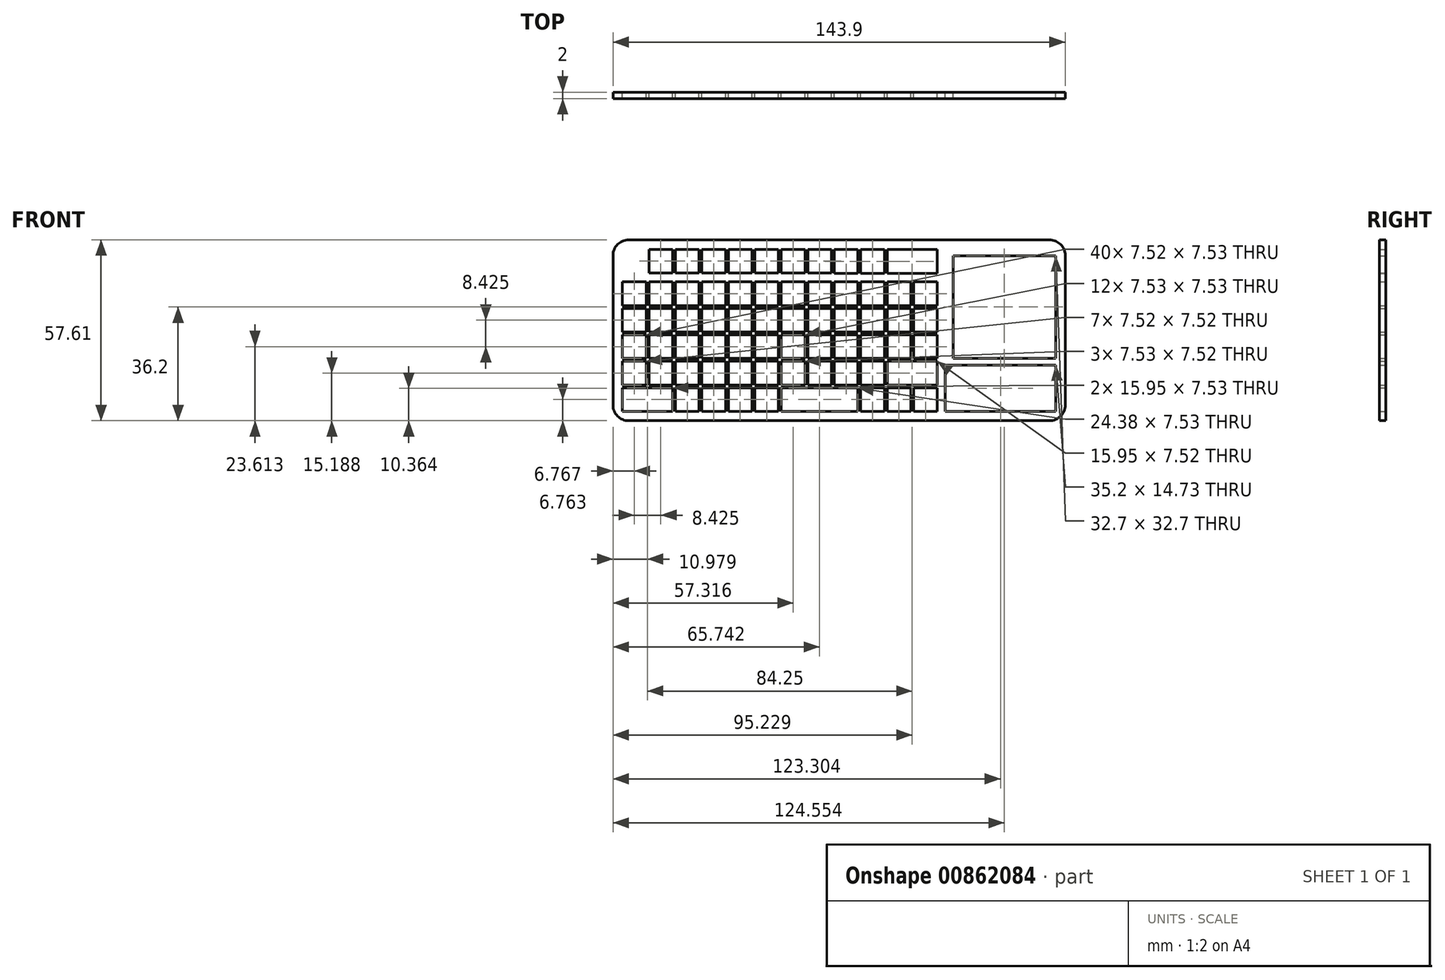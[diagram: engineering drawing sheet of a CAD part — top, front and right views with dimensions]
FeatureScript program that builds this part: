
annotation { "Feature Type Name" : "Feature", "Feature Type Description" : "" }
export const myFeature = defineFeature(function(context is Context, id is Id, definition is map)
    precondition{}
    {
        {
            var Q0;
            Q0=qCreatedBy(makeId("Front.planeOp"),FACE);
            var sketch = newSketch(context, id + "F0", { "sketchPlane" : qUnion([Q0])});
            skLineSegment(sketch, "E0.bottom", {"start": v(-54.97, 7.52) * mm, "end": v(-47.44, 7.52) * mm});
            skLineSegment(sketch, "E0.top", {"start": v(-54.97, 0) * mm, "end": v(-47.44, 0) * mm});
            skLineSegment(sketch, "E0.left", {"start": v(-54.97, 7.52) * mm, "end": v(-54.97, 0) * mm});
            skLineSegment(sketch, "E0.right", {"start": v(-47.44, 7.52) * mm, "end": v(-47.44, 0) * mm});
            skLineSegment(sketch, "E1.bottom", {"start": v(-46.54, 7.52) * mm, "end": v(-39.02, 7.52) * mm});
            skLineSegment(sketch, "E1.top", {"start": v(-46.54, 0) * mm, "end": v(-39.02, 0) * mm});
            skLineSegment(sketch, "E1.left", {"start": v(-46.54, 7.52) * mm, "end": v(-46.54, 0) * mm});
            skLineSegment(sketch, "E1.right", {"start": v(-39.02, 7.52) * mm, "end": v(-39.02, 0) * mm});
            skLineSegment(sketch, "E2.bottom", {"start": v(-29.7, 7.52) * mm, "end": v(-22.17, 7.52) * mm});
            skLineSegment(sketch, "E2.top", {"start": v(-29.7, 0) * mm, "end": v(-22.17, 0) * mm});
            skLineSegment(sketch, "E2.left", {"start": v(-29.7, 7.52) * mm, "end": v(-29.7, 0) * mm});
            skLineSegment(sketch, "E2.right", {"start": v(-22.17, 7.52) * mm, "end": v(-22.17, 0) * mm});
            skLineSegment(sketch, "E3.bottom", {"start": v(-38.12, 7.52) * mm, "end": v(-30.6, 7.52) * mm});
            skLineSegment(sketch, "E3.top", {"start": v(-38.12, 0) * mm, "end": v(-30.6, 0) * mm});
            skLineSegment(sketch, "E3.left", {"start": v(-38.12, 7.52) * mm, "end": v(-38.12, 0) * mm});
            skLineSegment(sketch, "E3.right", {"start": v(-30.6, 7.52) * mm, "end": v(-30.6, 0) * mm});
            skLineSegment(sketch, "E4.bottom", {"start": v(-21.27, 7.53) * mm, "end": v(-13.74, 7.53) * mm});
            skLineSegment(sketch, "E4.top", {"start": v(-21.27, 0) * mm, "end": v(-13.74, 0) * mm});
            skLineSegment(sketch, "E4.left", {"start": v(-21.27, 7.52) * mm, "end": v(-21.27, 0) * mm});
            skLineSegment(sketch, "E4.right", {"start": v(-13.74, 7.52) * mm, "end": v(-13.74, 0) * mm});
            skLineSegment(sketch, "E5.bottom", {"start": v(-12.84, 7.52) * mm, "end": v(-5.32, 7.52) * mm});
            skLineSegment(sketch, "E5.top", {"start": v(-12.84, 0) * mm, "end": v(-5.32, 0) * mm});
            skLineSegment(sketch, "E5.left", {"start": v(-12.84, 7.52) * mm, "end": v(-12.84, 0) * mm});
            skLineSegment(sketch, "E5.right", {"start": v(-5.32, 7.52) * mm, "end": v(-5.32, 0) * mm});
            skLineSegment(sketch, "E6.bottom", {"start": v(4, 7.52) * mm, "end": v(11.53, 7.52) * mm});
            skLineSegment(sketch, "E6.top", {"start": v(4, 0) * mm, "end": v(11.53, 0) * mm});
            skLineSegment(sketch, "E6.left", {"start": v(4, 7.52) * mm, "end": v(4, 0) * mm});
            skLineSegment(sketch, "E6.right", {"start": v(11.53, 7.53) * mm, "end": v(11.53, 0) * mm});
            skLineSegment(sketch, "E7.bottom", {"start": v(-4.42, 7.52) * mm, "end": v(3.1, 7.52) * mm});
            skLineSegment(sketch, "E7.top", {"start": v(-4.42, 0) * mm, "end": v(3.1, 0) * mm});
            skLineSegment(sketch, "E7.left", {"start": v(-4.42, 7.52) * mm, "end": v(-4.42, 0) * mm});
            skLineSegment(sketch, "E7.right", {"start": v(3.1, 7.53) * mm, "end": v(3.1, 0) * mm});
            skLineSegment(sketch, "E8.bottom", {"start": v(12.43, 7.52) * mm, "end": v(19.96, 7.52) * mm});
            skLineSegment(sketch, "E8.top", {"start": v(12.43, 0) * mm, "end": v(19.96, 0) * mm});
            skLineSegment(sketch, "E8.left", {"start": v(12.43, 7.52) * mm, "end": v(12.43, 0) * mm});
            skLineSegment(sketch, "E8.right", {"start": v(19.96, 7.52) * mm, "end": v(19.96, 0) * mm});
            skLineSegment(sketch, "E9.bottom", {"start": v(20.86, 7.52) * mm, "end": v(28.38, 7.52) * mm});
            skLineSegment(sketch, "E9.top", {"start": v(20.86, 0) * mm, "end": v(28.38, 0) * mm});
            skLineSegment(sketch, "E9.left", {"start": v(20.86, 7.52) * mm, "end": v(20.86, 0) * mm});
            skLineSegment(sketch, "E9.right", {"start": v(28.38, 7.52) * mm, "end": v(28.38, 0) * mm});
            skLineSegment(sketch, "E10.bottom", {"start": v(37.7, 7.52) * mm, "end": v(45.23, 7.52) * mm});
            skLineSegment(sketch, "E10.top", {"start": v(37.7, 0) * mm, "end": v(45.23, 0) * mm});
            skLineSegment(sketch, "E10.left", {"start": v(37.7, 7.52) * mm, "end": v(37.7, 0) * mm});
            skLineSegment(sketch, "E10.right", {"start": v(45.23, 7.52) * mm, "end": v(45.23, 0) * mm});
            skLineSegment(sketch, "E11.bottom", {"start": v(29.28, 7.53) * mm, "end": v(36.8, 7.53) * mm});
            skLineSegment(sketch, "E11.top", {"start": v(29.28, 0) * mm, "end": v(36.8, 0) * mm});
            skLineSegment(sketch, "E11.left", {"start": v(29.28, 7.53) * mm, "end": v(29.28, 0) * mm});
            skLineSegment(sketch, "E11.right", {"start": v(36.8, 7.52) * mm, "end": v(36.8, 0) * mm});
            skLineSegment(sketch, "E12.bottom", {"start": v(-54.97, -0.9) * mm, "end": v(-47.44, -0.9) * mm});
            skLineSegment(sketch, "E12.top", {"start": v(-54.97, -8.42) * mm, "end": v(-47.44, -8.42) * mm});
            skLineSegment(sketch, "E12.left", {"start": v(-54.97, -0.9) * mm, "end": v(-54.97, -8.43) * mm});
            skLineSegment(sketch, "E12.right", {"start": v(-47.44, -0.9) * mm, "end": v(-47.44, -8.42) * mm});
            skLineSegment(sketch, "E13.bottom", {"start": v(-46.54, -0.9) * mm, "end": v(-39.02, -0.9) * mm});
            skLineSegment(sketch, "E13.top", {"start": v(-46.54, -8.42) * mm, "end": v(-39.02, -8.42) * mm});
            skLineSegment(sketch, "E13.left", {"start": v(-46.54, -0.9) * mm, "end": v(-46.54, -8.42) * mm});
            skLineSegment(sketch, "E13.right", {"start": v(-39.02, -0.9) * mm, "end": v(-39.02, -8.42) * mm});
            skLineSegment(sketch, "E14.bottom", {"start": v(-29.7, -0.9) * mm, "end": v(-22.17, -0.9) * mm});
            skLineSegment(sketch, "E14.top", {"start": v(-29.7, -8.42) * mm, "end": v(-22.17, -8.42) * mm});
            skLineSegment(sketch, "E14.left", {"start": v(-29.7, -0.9) * mm, "end": v(-29.7, -8.42) * mm});
            skLineSegment(sketch, "E14.right", {"start": v(-22.17, -0.9) * mm, "end": v(-22.17, -8.42) * mm});
            skLineSegment(sketch, "E15.bottom", {"start": v(-38.12, -0.9) * mm, "end": v(-30.6, -0.9) * mm});
            skLineSegment(sketch, "E15.top", {"start": v(-38.12, -8.42) * mm, "end": v(-30.6, -8.42) * mm});
            skLineSegment(sketch, "E15.left", {"start": v(-38.12, -0.9) * mm, "end": v(-38.12, -8.42) * mm});
            skLineSegment(sketch, "E15.right", {"start": v(-30.6, -0.9) * mm, "end": v(-30.6, -8.42) * mm});
            skLineSegment(sketch, "E16.bottom", {"start": v(-21.27, -0.9) * mm, "end": v(-13.74, -0.9) * mm});
            skLineSegment(sketch, "E16.top", {"start": v(-21.27, -8.42) * mm, "end": v(-13.74, -8.42) * mm});
            skLineSegment(sketch, "E16.left", {"start": v(-21.27, -0.9) * mm, "end": v(-21.27, -8.42) * mm});
            skLineSegment(sketch, "E16.right", {"start": v(-13.74, -0.9) * mm, "end": v(-13.74, -8.42) * mm});
            skLineSegment(sketch, "E17.bottom", {"start": v(-12.84, -0.9) * mm, "end": v(-5.32, -0.9) * mm});
            skLineSegment(sketch, "E17.top", {"start": v(-12.84, -8.42) * mm, "end": v(-5.32, -8.42) * mm});
            skLineSegment(sketch, "E17.left", {"start": v(-12.84, -0.9) * mm, "end": v(-12.84, -8.42) * mm});
            skLineSegment(sketch, "E17.right", {"start": v(-5.32, -0.9) * mm, "end": v(-5.32, -8.42) * mm});
            skLineSegment(sketch, "E18.bottom", {"start": v(4, -0.9) * mm, "end": v(11.53, -0.9) * mm});
            skLineSegment(sketch, "E18.top", {"start": v(4, -8.42) * mm, "end": v(11.53, -8.42) * mm});
            skLineSegment(sketch, "E18.left", {"start": v(4, -0.9) * mm, "end": v(4, -8.42) * mm});
            skLineSegment(sketch, "E18.right", {"start": v(11.53, -0.9) * mm, "end": v(11.53, -8.42) * mm});
            skLineSegment(sketch, "E19.bottom", {"start": v(-4.42, -0.9) * mm, "end": v(3.1, -0.9) * mm});
            skLineSegment(sketch, "E19.top", {"start": v(-4.42, -8.42) * mm, "end": v(3.1, -8.42) * mm});
            skLineSegment(sketch, "E19.left", {"start": v(-4.42, -0.9) * mm, "end": v(-4.42, -8.42) * mm});
            skLineSegment(sketch, "E19.right", {"start": v(3.1, -0.9) * mm, "end": v(3.1, -8.42) * mm});
            skLineSegment(sketch, "E20.bottom", {"start": v(12.43, -0.9) * mm, "end": v(19.96, -0.9) * mm});
            skLineSegment(sketch, "E20.top", {"start": v(12.43, -8.42) * mm, "end": v(19.96, -8.42) * mm});
            skLineSegment(sketch, "E20.left", {"start": v(12.43, -0.9) * mm, "end": v(12.43, -8.42) * mm});
            skLineSegment(sketch, "E20.right", {"start": v(19.96, -0.9) * mm, "end": v(19.96, -8.42) * mm});
            skLineSegment(sketch, "E21.bottom", {"start": v(20.86, -0.9) * mm, "end": v(28.38, -0.9) * mm});
            skLineSegment(sketch, "E21.top", {"start": v(20.86, -8.42) * mm, "end": v(28.38, -8.42) * mm});
            skLineSegment(sketch, "E21.left", {"start": v(20.86, -0.9) * mm, "end": v(20.86, -8.42) * mm});
            skLineSegment(sketch, "E21.right", {"start": v(28.38, -0.9) * mm, "end": v(28.38, -8.42) * mm});
            skLineSegment(sketch, "E22.bottom", {"start": v(37.7, -0.9) * mm, "end": v(45.23, -0.9) * mm});
            skLineSegment(sketch, "E22.top", {"start": v(37.7, -8.42) * mm, "end": v(45.23, -8.42) * mm});
            skLineSegment(sketch, "E22.left", {"start": v(37.7, -0.9) * mm, "end": v(37.7, -8.42) * mm});
            skLineSegment(sketch, "E22.right", {"start": v(45.23, -0.9) * mm, "end": v(45.23, -8.42) * mm});
            skLineSegment(sketch, "E23.bottom", {"start": v(29.28, -0.9) * mm, "end": v(36.8, -0.9) * mm});
            skLineSegment(sketch, "E23.top", {"start": v(29.28, -8.42) * mm, "end": v(36.8, -8.42) * mm});
            skLineSegment(sketch, "E23.left", {"start": v(29.28, -0.9) * mm, "end": v(29.28, -8.42) * mm});
            skLineSegment(sketch, "E23.right", {"start": v(36.8, -0.9) * mm, "end": v(36.8, -8.42) * mm});
            skLineSegment(sketch, "E24", {"start": v(-54.97, -8.42) * mm, "end": v(45.23, -8.42) * mm});
            skLineSegment(sketch, "E25.bottom", {"start": v(-54.97, -9.32) * mm, "end": v(-47.44, -9.32) * mm});
            skLineSegment(sketch, "E25.top", {"start": v(-54.97, -16.85) * mm, "end": v(-47.44, -16.85) * mm});
            skLineSegment(sketch, "E25.left", {"start": v(-54.97, -9.32) * mm, "end": v(-54.97, -16.85) * mm});
            skLineSegment(sketch, "E25.right", {"start": v(-47.44, -9.32) * mm, "end": v(-47.44, -16.85) * mm});
            skLineSegment(sketch, "E26.bottom", {"start": v(-46.54, -9.32) * mm, "end": v(-39.02, -9.32) * mm});
            skLineSegment(sketch, "E26.top", {"start": v(-46.54, -16.85) * mm, "end": v(-39.02, -16.85) * mm});
            skLineSegment(sketch, "E26.left", {"start": v(-46.54, -9.32) * mm, "end": v(-46.54, -16.85) * mm});
            skLineSegment(sketch, "E26.right", {"start": v(-39.02, -9.32) * mm, "end": v(-39.02, -16.85) * mm});
            skLineSegment(sketch, "E27.bottom", {"start": v(-29.7, -9.32) * mm, "end": v(-22.17, -9.32) * mm});
            skLineSegment(sketch, "E27.top", {"start": v(-29.7, -16.85) * mm, "end": v(-22.17, -16.85) * mm});
            skLineSegment(sketch, "E27.left", {"start": v(-29.7, -9.32) * mm, "end": v(-29.7, -16.85) * mm});
            skLineSegment(sketch, "E27.right", {"start": v(-22.17, -9.32) * mm, "end": v(-22.17, -16.85) * mm});
            skLineSegment(sketch, "E28.bottom", {"start": v(-38.12, -9.32) * mm, "end": v(-30.6, -9.32) * mm});
            skLineSegment(sketch, "E28.top", {"start": v(-38.12, -16.85) * mm, "end": v(-30.6, -16.85) * mm});
            skLineSegment(sketch, "E28.left", {"start": v(-38.12, -9.32) * mm, "end": v(-38.12, -16.85) * mm});
            skLineSegment(sketch, "E28.right", {"start": v(-30.6, -9.32) * mm, "end": v(-30.6, -16.85) * mm});
            skLineSegment(sketch, "E29.bottom", {"start": v(-21.27, -9.32) * mm, "end": v(-13.74, -9.32) * mm});
            skLineSegment(sketch, "E29.top", {"start": v(-21.27, -16.85) * mm, "end": v(-13.74, -16.85) * mm});
            skLineSegment(sketch, "E29.left", {"start": v(-21.27, -9.32) * mm, "end": v(-21.27, -16.85) * mm});
            skLineSegment(sketch, "E29.right", {"start": v(-13.74, -9.32) * mm, "end": v(-13.74, -16.85) * mm});
            skLineSegment(sketch, "E30.bottom", {"start": v(-12.84, -9.32) * mm, "end": v(-5.32, -9.32) * mm});
            skLineSegment(sketch, "E30.top", {"start": v(-12.84, -16.85) * mm, "end": v(-5.32, -16.85) * mm});
            skLineSegment(sketch, "E30.left", {"start": v(-12.84, -9.32) * mm, "end": v(-12.84, -16.85) * mm});
            skLineSegment(sketch, "E30.right", {"start": v(-5.32, -9.32) * mm, "end": v(-5.32, -16.85) * mm});
            skLineSegment(sketch, "E31.bottom", {"start": v(4, -9.32) * mm, "end": v(11.53, -9.32) * mm});
            skLineSegment(sketch, "E31.top", {"start": v(4, -16.85) * mm, "end": v(11.53, -16.85) * mm});
            skLineSegment(sketch, "E31.left", {"start": v(4, -9.32) * mm, "end": v(4, -16.85) * mm});
            skLineSegment(sketch, "E31.right", {"start": v(11.53, -9.32) * mm, "end": v(11.53, -16.85) * mm});
            skLineSegment(sketch, "E32.bottom", {"start": v(-4.42, -9.32) * mm, "end": v(3.1, -9.32) * mm});
            skLineSegment(sketch, "E32.top", {"start": v(-4.42, -16.85) * mm, "end": v(3.1, -16.85) * mm});
            skLineSegment(sketch, "E32.left", {"start": v(-4.42, -9.32) * mm, "end": v(-4.42, -16.85) * mm});
            skLineSegment(sketch, "E32.right", {"start": v(3.1, -9.32) * mm, "end": v(3.1, -16.85) * mm});
            skLineSegment(sketch, "E33.bottom", {"start": v(12.43, -9.32) * mm, "end": v(19.96, -9.32) * mm});
            skLineSegment(sketch, "E33.top", {"start": v(12.43, -16.85) * mm, "end": v(19.96, -16.85) * mm});
            skLineSegment(sketch, "E33.left", {"start": v(12.43, -9.32) * mm, "end": v(12.43, -16.85) * mm});
            skLineSegment(sketch, "E33.right", {"start": v(19.96, -9.32) * mm, "end": v(19.96, -16.85) * mm});
            skLineSegment(sketch, "E34.bottom", {"start": v(20.86, -9.32) * mm, "end": v(28.38, -9.32) * mm});
            skLineSegment(sketch, "E34.top", {"start": v(20.86, -16.85) * mm, "end": v(28.38, -16.85) * mm});
            skLineSegment(sketch, "E34.left", {"start": v(20.86, -9.32) * mm, "end": v(20.86, -16.85) * mm});
            skLineSegment(sketch, "E34.right", {"start": v(28.38, -9.32) * mm, "end": v(28.38, -16.85) * mm});
            skLineSegment(sketch, "E35.bottom", {"start": v(37.7, -9.32) * mm, "end": v(45.23, -9.32) * mm});
            skLineSegment(sketch, "E35.top", {"start": v(37.7, -16.85) * mm, "end": v(45.23, -16.85) * mm});
            skLineSegment(sketch, "E35.left", {"start": v(37.7, -9.32) * mm, "end": v(37.7, -16.85) * mm});
            skLineSegment(sketch, "E35.right", {"start": v(45.23, -9.32) * mm, "end": v(45.23, -16.85) * mm});
            skLineSegment(sketch, "E36.bottom", {"start": v(29.28, -9.32) * mm, "end": v(36.8, -9.32) * mm});
            skLineSegment(sketch, "E36.top", {"start": v(29.28, -16.85) * mm, "end": v(36.8, -16.85) * mm});
            skLineSegment(sketch, "E36.left", {"start": v(29.28, -9.32) * mm, "end": v(29.28, -16.85) * mm});
            skLineSegment(sketch, "E36.right", {"start": v(36.8, -9.32) * mm, "end": v(36.8, -16.85) * mm});
            skLineSegment(sketch, "E37", {"start": v(-54.97, -16.85) * mm, "end": v(45.23, -16.85) * mm});
            skLineSegment(sketch, "E38.bottom", {"start": v(-54.97, -17.75) * mm, "end": v(-47.44, -17.75) * mm});
            skLineSegment(sketch, "E38.top", {"start": v(-54.97, -25.27) * mm, "end": v(-47.44, -25.27) * mm});
            skLineSegment(sketch, "E38.left", {"start": v(-54.97, -17.75) * mm, "end": v(-54.97, -25.27) * mm});
            skLineSegment(sketch, "E38.right", {"start": v(-47.44, -17.75) * mm, "end": v(-47.44, -25.27) * mm});
            skLineSegment(sketch, "E39.bottom", {"start": v(-46.54, -17.75) * mm, "end": v(-39.02, -17.75) * mm});
            skLineSegment(sketch, "E39.top", {"start": v(-46.54, -25.27) * mm, "end": v(-39.02, -25.27) * mm});
            skLineSegment(sketch, "E39.left", {"start": v(-46.54, -17.75) * mm, "end": v(-46.54, -25.28) * mm});
            skLineSegment(sketch, "E39.right", {"start": v(-39.02, -17.75) * mm, "end": v(-39.02, -25.28) * mm});
            skLineSegment(sketch, "E40.bottom", {"start": v(-29.7, -17.75) * mm, "end": v(-22.17, -17.75) * mm});
            skLineSegment(sketch, "E40.top", {"start": v(-29.7, -25.27) * mm, "end": v(-22.17, -25.27) * mm});
            skLineSegment(sketch, "E40.left", {"start": v(-29.7, -17.75) * mm, "end": v(-29.7, -25.27) * mm});
            skLineSegment(sketch, "E40.right", {"start": v(-22.17, -17.75) * mm, "end": v(-22.17, -25.27) * mm});
            skLineSegment(sketch, "E41.bottom", {"start": v(-38.12, -17.75) * mm, "end": v(-30.6, -17.75) * mm});
            skLineSegment(sketch, "E41.top", {"start": v(-38.12, -25.27) * mm, "end": v(-30.6, -25.27) * mm});
            skLineSegment(sketch, "E41.left", {"start": v(-38.12, -17.75) * mm, "end": v(-38.12, -25.27) * mm});
            skLineSegment(sketch, "E41.right", {"start": v(-30.6, -17.75) * mm, "end": v(-30.6, -25.27) * mm});
            skLineSegment(sketch, "E42.bottom", {"start": v(-21.27, -17.75) * mm, "end": v(-13.74, -17.75) * mm});
            skLineSegment(sketch, "E42.top", {"start": v(-21.27, -25.27) * mm, "end": v(-13.74, -25.27) * mm});
            skLineSegment(sketch, "E42.left", {"start": v(-21.27, -17.75) * mm, "end": v(-21.27, -25.27) * mm});
            skLineSegment(sketch, "E42.right", {"start": v(-13.74, -17.75) * mm, "end": v(-13.74, -25.27) * mm});
            skLineSegment(sketch, "E43.bottom", {"start": v(-12.84, -17.75) * mm, "end": v(-5.32, -17.75) * mm});
            skLineSegment(sketch, "E43.top", {"start": v(-12.84, -25.27) * mm, "end": v(-5.32, -25.27) * mm});
            skLineSegment(sketch, "E43.left", {"start": v(-12.84, -17.75) * mm, "end": v(-12.84, -25.27) * mm});
            skLineSegment(sketch, "E43.right", {"start": v(-5.32, -17.75) * mm, "end": v(-5.32, -25.27) * mm});
            skLineSegment(sketch, "E44.bottom", {"start": v(4, -17.75) * mm, "end": v(11.53, -17.75) * mm});
            skLineSegment(sketch, "E44.top", {"start": v(4, -25.27) * mm, "end": v(11.53, -25.27) * mm});
            skLineSegment(sketch, "E44.left", {"start": v(4, -17.75) * mm, "end": v(4, -25.27) * mm});
            skLineSegment(sketch, "E44.right", {"start": v(11.53, -17.75) * mm, "end": v(11.53, -25.27) * mm});
            skLineSegment(sketch, "E45.bottom", {"start": v(-4.42, -17.75) * mm, "end": v(3.1, -17.75) * mm});
            skLineSegment(sketch, "E45.top", {"start": v(-4.42, -25.27) * mm, "end": v(3.1, -25.27) * mm});
            skLineSegment(sketch, "E45.left", {"start": v(-4.42, -17.75) * mm, "end": v(-4.42, -25.27) * mm});
            skLineSegment(sketch, "E45.right", {"start": v(3.1, -17.75) * mm, "end": v(3.1, -25.27) * mm});
            skLineSegment(sketch, "E46.bottom", {"start": v(12.43, -17.75) * mm, "end": v(19.96, -17.75) * mm});
            skLineSegment(sketch, "E46.top", {"start": v(12.43, -25.27) * mm, "end": v(19.96, -25.27) * mm});
            skLineSegment(sketch, "E46.left", {"start": v(12.43, -17.75) * mm, "end": v(12.43, -25.27) * mm});
            skLineSegment(sketch, "E46.right", {"start": v(19.96, -17.75) * mm, "end": v(19.96, -25.27) * mm});
            skLineSegment(sketch, "E47.bottom", {"start": v(20.86, -17.75) * mm, "end": v(28.38, -17.75) * mm});
            skLineSegment(sketch, "E47.top", {"start": v(20.86, -25.27) * mm, "end": v(28.38, -25.27) * mm});
            skLineSegment(sketch, "E47.left", {"start": v(20.86, -17.75) * mm, "end": v(20.86, -25.27) * mm});
            skLineSegment(sketch, "E47.right", {"start": v(28.38, -17.75) * mm, "end": v(28.38, -25.27) * mm});
            skLineSegment(sketch, "E48.top", {"start": v(37.7, -25.27) * mm, "end": v(45.23, -25.27) * mm});
            skLineSegment(sketch, "E48.right", {"start": v(45.23, -17.75) * mm, "end": v(45.23, -25.28) * mm});
            skLineSegment(sketch, "E49.top", {"start": v(29.28, -25.27) * mm, "end": v(36.8, -25.27) * mm});
            skLineSegment(sketch, "E49.left", {"start": v(29.28, -17.75) * mm, "end": v(29.28, -25.27) * mm});
            skLineSegment(sketch, "E50", {"start": v(-54.97, -25.27) * mm, "end": v(45.23, -25.27) * mm});
            skLineSegment(sketch, "E51.top", {"start": v(-54.97, -33.7) * mm, "end": v(-47.44, -33.7) * mm});
            skLineSegment(sketch, "E51.left", {"start": v(-54.97, -26.17) * mm, "end": v(-54.97, -33.7) * mm});
            skLineSegment(sketch, "E52.top", {"start": v(-46.54, -33.7) * mm, "end": v(-39.02, -33.7) * mm});
            skLineSegment(sketch, "E52.right", {"start": v(-39.02, -26.17) * mm, "end": v(-39.02, -33.7) * mm});
            skLineSegment(sketch, "E53.bottom", {"start": v(-29.7, -26.17) * mm, "end": v(-22.17, -26.17) * mm});
            skLineSegment(sketch, "E53.top", {"start": v(-29.7, -33.7) * mm, "end": v(-22.17, -33.7) * mm});
            skLineSegment(sketch, "E53.left", {"start": v(-29.7, -26.17) * mm, "end": v(-29.7, -33.7) * mm});
            skLineSegment(sketch, "E53.right", {"start": v(-22.17, -26.17) * mm, "end": v(-22.17, -33.7) * mm});
            skLineSegment(sketch, "E54.bottom", {"start": v(-38.12, -26.17) * mm, "end": v(-30.6, -26.17) * mm});
            skLineSegment(sketch, "E54.top", {"start": v(-38.12, -33.7) * mm, "end": v(-30.6, -33.7) * mm});
            skLineSegment(sketch, "E54.left", {"start": v(-38.12, -26.17) * mm, "end": v(-38.12, -33.7) * mm});
            skLineSegment(sketch, "E54.right", {"start": v(-30.6, -26.17) * mm, "end": v(-30.6, -33.7) * mm});
            skLineSegment(sketch, "E55.bottom", {"start": v(-21.27, -26.17) * mm, "end": v(-13.74, -26.17) * mm});
            skLineSegment(sketch, "E55.top", {"start": v(-21.27, -33.7) * mm, "end": v(-13.74, -33.7) * mm});
            skLineSegment(sketch, "E55.left", {"start": v(-21.27, -26.17) * mm, "end": v(-21.27, -33.7) * mm});
            skLineSegment(sketch, "E55.right", {"start": v(-13.74, -26.17) * mm, "end": v(-13.74, -33.7) * mm});
            skLineSegment(sketch, "E56.bottom", {"start": v(-12.84, -26.17) * mm, "end": v(-5.32, -26.17) * mm});
            skLineSegment(sketch, "E56.top", {"start": v(-12.84, -33.7) * mm, "end": v(-5.32, -33.7) * mm});
            skLineSegment(sketch, "E56.left", {"start": v(-12.84, -26.17) * mm, "end": v(-12.84, -33.7) * mm});
            skLineSegment(sketch, "E56.right", {"start": v(-5.32, -26.17) * mm, "end": v(-5.32, -33.7) * mm});
            skLineSegment(sketch, "E57.top", {"start": v(4, -33.7) * mm, "end": v(11.53, -33.7) * mm});
            skLineSegment(sketch, "E58.top", {"start": v(-4.42, -33.7) * mm, "end": v(3.1, -33.7) * mm});
            skLineSegment(sketch, "E58.left", {"start": v(-4.42, -26.17) * mm, "end": v(-4.42, -33.7) * mm});
            skLineSegment(sketch, "E59.top", {"start": v(12.43, -33.7) * mm, "end": v(19.96, -33.7) * mm});
            skLineSegment(sketch, "E59.right", {"start": v(19.96, -26.17) * mm, "end": v(19.96, -33.7) * mm});
            skLineSegment(sketch, "E60.bottom", {"start": v(20.86, -26.17) * mm, "end": v(28.38, -26.17) * mm});
            skLineSegment(sketch, "E60.top", {"start": v(20.86, -33.7) * mm, "end": v(28.38, -33.7) * mm});
            skLineSegment(sketch, "E60.left", {"start": v(20.86, -26.17) * mm, "end": v(20.86, -33.7) * mm});
            skLineSegment(sketch, "E60.right", {"start": v(28.38, -26.17) * mm, "end": v(28.38, -33.7) * mm});
            skLineSegment(sketch, "E61.bottom", {"start": v(37.7, -26.17) * mm, "end": v(45.23, -26.17) * mm});
            skLineSegment(sketch, "E61.top", {"start": v(37.7, -33.7) * mm, "end": v(45.23, -33.7) * mm});
            skLineSegment(sketch, "E61.left", {"start": v(37.7, -26.17) * mm, "end": v(37.7, -33.7) * mm});
            skLineSegment(sketch, "E61.right", {"start": v(45.23, -26.17) * mm, "end": v(45.23, -33.7) * mm});
            skLineSegment(sketch, "E62.bottom", {"start": v(29.28, -26.17) * mm, "end": v(36.8, -26.18) * mm});
            skLineSegment(sketch, "E62.top", {"start": v(29.28, -33.7) * mm, "end": v(36.8, -33.7) * mm});
            skLineSegment(sketch, "E62.left", {"start": v(29.28, -26.17) * mm, "end": v(29.28, -33.7) * mm});
            skLineSegment(sketch, "E62.right", {"start": v(36.8, -26.17) * mm, "end": v(36.8, -33.7) * mm});
            skLineSegment(sketch, "E63", {"start": v(-54.97, -33.7) * mm, "end": v(45.23, -33.7) * mm});
            skLineSegment(sketch, "E64", {"start": v(45.23, 7.53) * mm, "end": v(45.23, -33.7) * mm});
            skLineSegment(sketch, "E65.bottom", {"start": v(-46.54, 17.9) * mm, "end": v(-39.02, 17.9) * mm});
            skLineSegment(sketch, "E65.top", {"start": v(-46.54, 10.38) * mm, "end": v(-39.02, 10.38) * mm});
            skLineSegment(sketch, "E65.left", {"start": v(-46.54, 17.9) * mm, "end": v(-46.54, 10.38) * mm});
            skLineSegment(sketch, "E65.right", {"start": v(-39.02, 17.9) * mm, "end": v(-39.02, 10.38) * mm});
            skLineSegment(sketch, "E66.bottom", {"start": v(-29.7, 17.9) * mm, "end": v(-22.17, 17.9) * mm});
            skLineSegment(sketch, "E66.top", {"start": v(-29.7, 10.38) * mm, "end": v(-22.17, 10.38) * mm});
            skLineSegment(sketch, "E66.left", {"start": v(-29.7, 17.9) * mm, "end": v(-29.7, 10.38) * mm});
            skLineSegment(sketch, "E66.right", {"start": v(-22.17, 17.9) * mm, "end": v(-22.17, 10.38) * mm});
            skLineSegment(sketch, "E67.bottom", {"start": v(-38.12, 17.9) * mm, "end": v(-30.6, 17.9) * mm});
            skLineSegment(sketch, "E67.top", {"start": v(-38.12, 10.38) * mm, "end": v(-30.6, 10.38) * mm});
            skLineSegment(sketch, "E67.left", {"start": v(-38.12, 17.9) * mm, "end": v(-38.12, 10.38) * mm});
            skLineSegment(sketch, "E67.right", {"start": v(-30.6, 17.9) * mm, "end": v(-30.6, 10.38) * mm});
            skLineSegment(sketch, "E68.bottom", {"start": v(-21.27, 17.9) * mm, "end": v(-13.74, 17.9) * mm});
            skLineSegment(sketch, "E68.top", {"start": v(-21.27, 10.38) * mm, "end": v(-13.74, 10.38) * mm});
            skLineSegment(sketch, "E68.left", {"start": v(-21.27, 17.9) * mm, "end": v(-21.27, 10.38) * mm});
            skLineSegment(sketch, "E68.right", {"start": v(-13.74, 17.9) * mm, "end": v(-13.74, 10.38) * mm});
            skLineSegment(sketch, "E69.bottom", {"start": v(-12.84, 17.9) * mm, "end": v(-5.32, 17.9) * mm});
            skLineSegment(sketch, "E69.top", {"start": v(-12.84, 10.38) * mm, "end": v(-5.32, 10.38) * mm});
            skLineSegment(sketch, "E69.left", {"start": v(-12.84, 17.9) * mm, "end": v(-12.84, 10.38) * mm});
            skLineSegment(sketch, "E69.right", {"start": v(-5.32, 17.9) * mm, "end": v(-5.32, 10.38) * mm});
            skLineSegment(sketch, "E70.bottom", {"start": v(4, 17.9) * mm, "end": v(11.53, 17.9) * mm});
            skLineSegment(sketch, "E70.top", {"start": v(4, 10.38) * mm, "end": v(11.53, 10.38) * mm});
            skLineSegment(sketch, "E70.left", {"start": v(4, 17.9) * mm, "end": v(4, 10.38) * mm});
            skLineSegment(sketch, "E70.right", {"start": v(11.53, 17.9) * mm, "end": v(11.53, 10.38) * mm});
            skLineSegment(sketch, "E71.bottom", {"start": v(-4.42, 17.9) * mm, "end": v(3.1, 17.9) * mm});
            skLineSegment(sketch, "E71.top", {"start": v(-4.42, 10.38) * mm, "end": v(3.1, 10.38) * mm});
            skLineSegment(sketch, "E71.left", {"start": v(-4.42, 17.9) * mm, "end": v(-4.42, 10.38) * mm});
            skLineSegment(sketch, "E71.right", {"start": v(3.1, 17.9) * mm, "end": v(3.1, 10.38) * mm});
            skLineSegment(sketch, "E72.bottom", {"start": v(12.43, 17.8) * mm, "end": v(19.96, 17.8) * mm});
            skLineSegment(sketch, "E72.top", {"start": v(12.43, 10.27) * mm, "end": v(19.96, 10.27) * mm});
            skLineSegment(sketch, "E72.left", {"start": v(12.43, 17.8) * mm, "end": v(12.43, 10.27) * mm});
            skLineSegment(sketch, "E72.right", {"start": v(19.96, 17.8) * mm, "end": v(19.96, 10.27) * mm});
            skLineSegment(sketch, "E73.bottom", {"start": v(20.86, 17.8) * mm, "end": v(28.38, 17.8) * mm});
            skLineSegment(sketch, "E73.top", {"start": v(20.86, 10.27) * mm, "end": v(28.38, 10.27) * mm});
            skLineSegment(sketch, "E73.left", {"start": v(20.86, 17.8) * mm, "end": v(20.86, 10.27) * mm});
            skLineSegment(sketch, "E73.right", {"start": v(28.38, 17.8) * mm, "end": v(28.38, 10.27) * mm});
            skLineSegment(sketch, "E74.bottom", {"start": v(37.7, 17.8) * mm, "end": v(45.23, 17.8) * mm});
            skLineSegment(sketch, "E74.top", {"start": v(37.7, 10.27) * mm, "end": v(45.23, 10.27) * mm});
            skLineSegment(sketch, "E74.right", {"start": v(45.23, 17.8) * mm, "end": v(45.23, 10.27) * mm});
            skLineSegment(sketch, "E75.bottom", {"start": v(29.28, 17.8) * mm, "end": v(36.8, 17.8) * mm});
            skLineSegment(sketch, "E75.top", {"start": v(29.28, 10.27) * mm, "end": v(36.8, 10.27) * mm});
            skLineSegment(sketch, "E75.left", {"start": v(29.28, 17.8) * mm, "end": v(29.28, 10.27) * mm});
            skLineSegment(sketch, "E76", {"start": v(-46.54, 10.38) * mm, "end": v(45.23, 10.27) * mm});
            skLineSegment(sketch, "E77", {"start": v(36.8, 17.8) * mm, "end": v(37.7, 17.8) * mm});
            skLineSegment(sketch, "E78", {"start": v(36.8, 10.27) * mm, "end": v(37.7, 10.27) * mm});
            skLineSegment(sketch, "E79", {"start": v(29.28, -17.75) * mm, "end": v(45.23, -17.75) * mm});
            skLineSegment(sketch, "E80", {"start": v(-54.97, -26.17) * mm, "end": v(-39.02, -26.17) * mm});
            skLineSegment(sketch, "E81", {"start": v(-4.42, -26.17) * mm, "end": v(19.96, -26.17) * mm});
            skLineSegment(sketch, "E82.bottom", {"start": v(50.23, 15.85) * mm, "end": v(82.93, 15.85) * mm});
            skLineSegment(sketch, "E82.top", {"start": v(50.23, -16.85) * mm, "end": v(82.93, -16.85) * mm});
            skLineSegment(sketch, "E82.left", {"start": v(50.23, 15.85) * mm, "end": v(50.23, -16.85) * mm});
            skLineSegment(sketch, "E82.right", {"start": v(82.93, 15.85) * mm, "end": v(82.93, -16.85) * mm});
            skLineSegment(sketch, "E83", {"start": v(50.23, -16.85) * mm, "end": v(45.23, -16.85) * mm});
            skLineSegment(sketch, "E84.bottom", {"start": v(-57.97, 20.9) * mm, "end": v(85.93, 20.9) * mm});
            skLineSegment(sketch, "E84.top", {"start": v(-57.97, -36.7) * mm, "end": v(85.93, -36.7) * mm});
            skLineSegment(sketch, "E84.left", {"start": v(-57.97, 20.9) * mm, "end": v(-57.97, -36.7) * mm});
            skLineSegment(sketch, "E84.right", {"start": v(85.93, 20.9) * mm, "end": v(85.93, -36.7) * mm});
            skLineSegment(sketch, "E85.bottom", {"start": v(47.73, -16.85) * mm, "end": v(82.93, -16.85) * mm});
            skLineSegment(sketch, "E86.bottom", {"start": v(47.73, -18.97) * mm, "end": v(82.93, -18.97) * mm});
            skLineSegment(sketch, "E86.top", {"start": v(47.73, -33.7) * mm, "end": v(82.93, -33.7) * mm});
            skLineSegment(sketch, "E86.left", {"start": v(47.73, -18.97) * mm, "end": v(47.73, -33.7) * mm});
            skLineSegment(sketch, "E86.right", {"start": v(82.93, -18.97) * mm, "end": v(82.93, -33.7) * mm});
            skLineSegment(sketch, "E87", {"start": v(47.73, -16.85) * mm, "end": v(47.73, -18.97) * mm});
            skSolve(sketch);
        }
        {
            var Q0;
            Q0 = qSketchRegion(id + "F0", true);
            extrude(context, id + "F1", {"entities" : qUnion([Q0]), "depth" : 2 * mm, "offsetDistance" : 25 * mm});
        }
        {
            var Q0;
            Q0=makeQuery(id+"F1.opExtrude","SWEPT_EDGE",EDGE,{"disambiguationData":[OSD([sQuery(id+"F0.wireOp",EDGE,"E84.bottom"),sQuery(id+"F0.wireOp",EDGE,"E84.left")])]});
            var Q1;
            Q1=makeQuery(id+"F1.opExtrude","SWEPT_EDGE",EDGE,{"disambiguationData":[OSD([sQuery(id+"F0.wireOp",EDGE,"E84.bottom"),sQuery(id+"F0.wireOp",EDGE,"E84.right")])]});
            var Q2;
            Q2=makeQuery(id+"F1.opExtrude","SWEPT_EDGE",EDGE,{"disambiguationData":[OSD([sQuery(id+"F0.wireOp",EDGE,"E84.top"),sQuery(id+"F0.wireOp",EDGE,"E84.left")])]});
            var Q3;
            Q3=makeQuery(id+"F1.opExtrude","SWEPT_EDGE",EDGE,{"disambiguationData":[OSD([sQuery(id+"F0.wireOp",EDGE,"E84.top"),sQuery(id+"F0.wireOp",EDGE,"E84.right")])]});
            fillet(context, id + "F2", {"entities" : qUnion([Q0, Q1, Q2, Q3]), "radius" : 5 * mm, "tangentPropagation" : true, "allowEdgeOverflow" : false});
        }
    });
